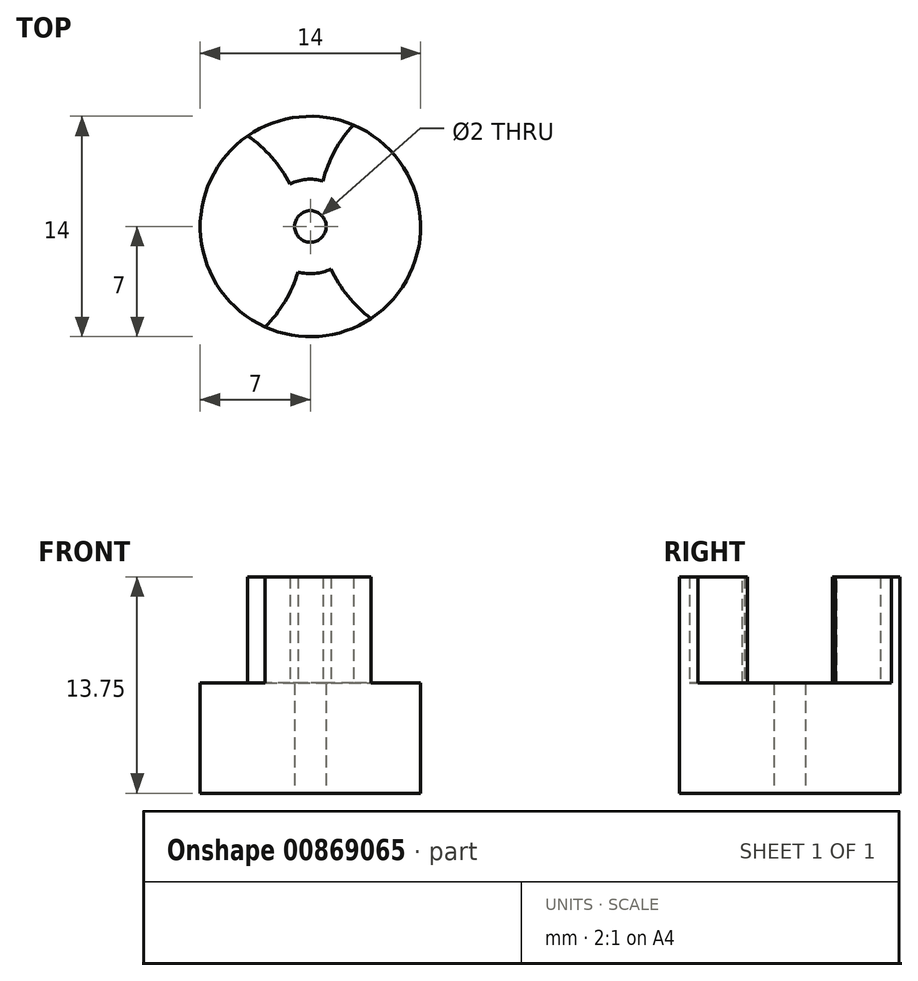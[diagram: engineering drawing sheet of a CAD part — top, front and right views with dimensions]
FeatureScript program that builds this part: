
annotation { "Feature Type Name" : "Feature", "Feature Type Description" : "" }
export const myFeature = defineFeature(function(context is Context, id is Id, definition is map)
    precondition{}
    {
        {
            var Q0;
            Q0=qCreatedBy(makeId("Top.planeOp"),FACE);
            var sketch = newSketch(context, id + "F0", { "sketchPlane" : qUnion([Q0])});
            skCircle(sketch, "E0", {"center": v(0, 0) * mm, "radius": 7 * mm});
            skSolve(sketch);
        }
        {
            var Q0;
            Q0 = qSketchRegion(id + "F0", true);
            extrude(context, id + "F1", {"entities" : qUnion([Q0]), "depth" : 7 * mm, "offsetDistance" : 25.4 * mm});
        }
        {
            var Q0;
            Q0=makeQuery(id+"F1.opExtrude","CAP_FACE",FACE,{"disambiguationData":[OSD([sQuery(id+"F0.wireOp",EDGE,"E0")])],"isStart":false});
            var sketch = newSketch(context, id + "F2", { "sketchPlane" : qUnion([Q0])});
            skCircle(sketch, "E1", {"center": v(0, 0) * mm, "radius": 3 * mm});
            skArc(sketch, "E2", {"start": v(-1.3, 2.7) * mm, "mid": v(-2.46, 4.4) * mm, "end": v(-3.99, 5.75) * mm});
            skArc(sketch, "E3", {"start": v(2.73, 6.45) * mm, "mid": v(1.54, 4.79) * mm, "end": v(0.79, 2.9) * mm});
            skLineSegment(sketch, "E4", {"start": v(-10.77, -0.98) * mm, "end": v(9.68, 0.88) * mm});
            skArc(sketch, "E5.MirrorCS", {"start": v(-0.79, -2.9) * mm, "mid": v(-1.62, -4.77) * mm, "end": v(-2.88, -6.38) * mm});
            skArc(sketch, "E6.MirrorCS", {"start": v(3.85, -5.84) * mm, "mid": v(2.39, -4.43) * mm, "end": v(1.3, -2.7) * mm});
            skArc(sketch, "E7", {"start": v(-2.88, -6.38) * mm, "mid": v(0.56, -6.98) * mm, "end": v(3.85, -5.84) * mm});
            skArc(sketch, "E8.trimOffspring", {"start": v(2.73, 6.45) * mm, "mid": v(-0.72, 6.96) * mm, "end": v(-3.99, 5.75) * mm});
            skSolve(sketch);
        }
        {
            var Q0;
            Q0 = qSketchRegion(id + "F2", true);
            extrude(context, id + "F3", {"entities" : qUnion([Q0]), "operationType" : NewBodyOperationType.ADD, "depth" : 6.75 * mm, "offsetDistance" : 25.4 * mm});
        }
        {
            var Q0;
            Q0=makeQuery(id+"F3.opExtrude","CAP_FACE",FACE,{"disambiguationData":[OSD([sQuery(id+"F2.wireOp",EDGE,"E1"),sQuery(id+"F2.wireOp",EDGE,"E2"),sQuery(id+"F2.wireOp",EDGE,"E3"),sQuery(id+"F2.wireOp",EDGE,"E5.MirrorCS"),sQuery(id+"F2.wireOp",EDGE,"E6.MirrorCS"),sQuery(id+"F2.wireOp",EDGE,"E7"),sQuery(id+"F2.wireOp",EDGE,"E8.trimOffspring")])],"isStart":false});
            var sketch = newSketch(context, id + "F4", { "sketchPlane" : qUnion([Q0])});
            skCircle(sketch, "E9", {"center": v(0, 0) * mm, "radius": 3 * mm});
            skSolve(sketch);
        }
        {
            var Q0;
            Q0 = qSketchRegion(id + "F4", true);
            extrude(context, id + "F5", {"entities" : qUnion([Q0]), "operationType" : NewBodyOperationType.REMOVE, "oppositeDirection" : true, "depth" : 6.75 * mm, "offsetDistance" : 25.4 * mm});
        }
        {
            var Q0;
            Q0=makeQuery(id+"F1.opExtrude","CAP_FACE",FACE,{"disambiguationData":[OSD([sQuery(id+"F0.wireOp",EDGE,"E0")])],"isStart":true});
            var sketch = newSketch(context, id + "F6", { "sketchPlane" : qUnion([Q0])});
            skCircle(sketch, "E10", {"center": v(0, 0) * mm, "radius": 1 * mm});
            skSolve(sketch);
        }
        {
            var Q0;
            Q0 = qSketchRegion(id + "F6", true);
            extrude(context, id + "F7", {"entities" : qUnion([Q0]), "operationType" : NewBodyOperationType.REMOVE, "endBound" : BoundingType.THROUGH_ALL, "oppositeDirection" : true, "depth" : 25.4 * mm, "offsetDistance" : 25.4 * mm});
        }
    });
